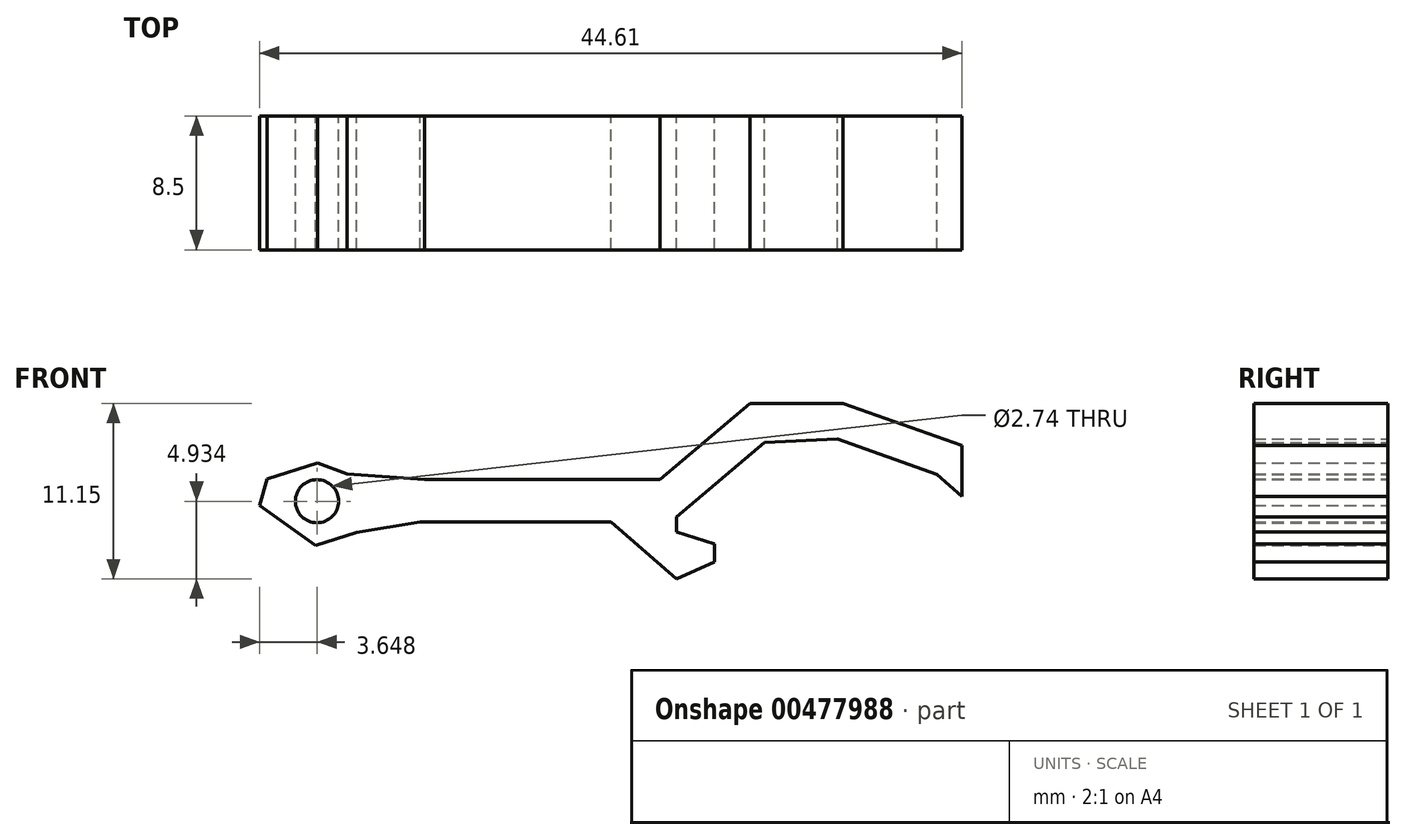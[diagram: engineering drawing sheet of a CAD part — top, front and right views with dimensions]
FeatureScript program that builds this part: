
annotation { "Feature Type Name" : "Feature", "Feature Type Description" : "" }
export const myFeature = defineFeature(function(context is Context, id is Id, definition is map)
    precondition{}
    {
        {
            var Q0;
            Q0=qCreatedBy(makeId("Front.planeOp"),FACE);
            var sketch = newSketch(context, id + "F0", { "sketchPlane" : qUnion([Q0])});
            skLineSegment(sketch, "E0", {"start": v(-10.83, -4.63) * mm, "end": v(-14.04, -5.62) * mm});
            skLineSegment(sketch, "E1", {"start": v(-14.04, -5.62) * mm, "end": v(-14.53, -7.32) * mm});
            skLineSegment(sketch, "E2", {"start": v(-14.53, -7.32) * mm, "end": v(-10.99, -9.86) * mm});
            skLineSegment(sketch, "E3", {"start": v(-10.99, -9.86) * mm, "end": v(-8.36, -9.03) * mm});
            skLineSegment(sketch, "E4", {"start": v(-8.96, -5.32) * mm, "end": v(-10.83, -4.63) * mm});
            skCircle(sketch, "E5", {"center": v(-10.88, -7.05) * mm, "radius": 1.37 * mm});
            skLineSegment(sketch, "E6", {"start": v(-8.36, -9.03) * mm, "end": v(-4.34, -8.35) * mm});
            skLineSegment(sketch, "E7", {"start": v(-8.96, -5.32) * mm, "end": v(-4.05, -5.65) * mm});
            skLineSegment(sketch, "E8", {"start": v(30.08, -3.5) * mm, "end": v(22.54, -0.83) * mm});
            skLineSegment(sketch, "E9", {"start": v(30.08, -6.74) * mm, "end": v(28.5, -5.34) * mm});
            skLineSegment(sketch, "E10", {"start": v(30.08, -3.5) * mm, "end": v(30.08, -6.74) * mm});
            skLineSegment(sketch, "E11", {"start": v(-4.34, -8.35) * mm, "end": v(7.78, -8.35) * mm});
            skLineSegment(sketch, "E12", {"start": v(11.94, -8.04) * mm, "end": v(11.94, -9) * mm});
            skLineSegment(sketch, "E13", {"start": v(11.94, -9) * mm, "end": v(14.37, -9.75) * mm});
            skLineSegment(sketch, "E14", {"start": v(14.37, -9.75) * mm, "end": v(14.37, -10.92) * mm});
            skLineSegment(sketch, "E15", {"start": v(14.37, -10.92) * mm, "end": v(11.94, -11.98) * mm});
            skLineSegment(sketch, "E16", {"start": v(11.94, -11.98) * mm, "end": v(7.78, -8.35) * mm});
            skLineSegment(sketch, "E17.0", {"start": v(28.5, -5.34) * mm, "end": v(22.17, -3.08) * mm});
            skLineSegment(sketch, "E18.0", {"start": v(22.17, -3.08) * mm, "end": v(17.54, -3.33) * mm});
            skLineSegment(sketch, "E19", {"start": v(11.94, -8.04) * mm, "end": v(17.54, -3.33) * mm});
            skLineSegment(sketch, "E20", {"start": v(-4.05, -5.65) * mm, "end": v(10.9, -5.65) * mm});
            skLineSegment(sketch, "E21", {"start": v(10.9, -5.65) * mm, "end": v(16.63, -0.83) * mm});
            skLineSegment(sketch, "E22", {"start": v(16.63, -0.83) * mm, "end": v(22.54, -0.83) * mm});
            skSolve(sketch);
        }
        {
            var Q0;
            Q0=makeQuery(id+"F0.imprint","IMPRINT",FACE,{"disambiguationData":[TD([[makeQuery(id+"F0.imprint","IMPRINT",EDGE,{"derivedFrom":sQuery(id+"F0.wireOp",EDGE,"E0")}),1.0]])]});
            extrude(context, id + "F1", {"entities" : qUnion([Q0]), "depth" : 8.5 * mm});
        }
    });
